# Revit family: Freestanding_Tub-American_Standard-Town_Square-2546004.020
name_source: partatom
category: Plumbing Fixtures
units: mm (PartAtom-declared; Revit-internal decimal feet)

## family parameters
Always vertical = No
Cut with Voids When Loaded = No
OmniClass Number = 23.45.05.14.21
OmniClass Title = Bathtubs
Part Type = Normal
Room Calculation Point = No
Round Connector Dimension = Use Diameter
Shared = Yes
Work Plane-Based = Yes

## types (1)
- 2546004.020
    Assembly Code = D2010510
    CSA B45.5-11 = Yes
    CW Connection = Yes
    CWFU = 3
    Cold Water Connection Diameter = 1/2"
    Default Elevation = 0"
    Description = Town Square® S Freestanding Tub High Gloss Acrylic
    Finish = High Gloss Acrylic-American Standard-020-White
    HW Connection = Yes
    HWFU = 3
    Height = 24 7/16"
    Hot Water Connection Diameter = 1/2"
    IAPMO Z124 = Yes
    Installation Type = Floor Mounted
    Length = 68"
    Manufacturer = American Standard
    Material = High Gloss Acrylic-American Standard-020-White
    Model = 2546004.020
    Price = Prices may vary. Please consult Manufacturer Representative for most up-to-date price list.
    Product Documentation Link = https://americanstandard.box.com
    Product Page URL = https://www.americanstandard-us.com
    Revised Date = 02/09/2022
    Shower = Yes
    Shower Connection Size = 1/2"
    Shower Width = 6"
    Shower void = 24 27/32"
    Supply Width = 4"
    Type Comments = Deck mount filler and overflow cover sold separately
    URL = https://www.americanstandard-us.com
    Vent Connection = No
    WFU = 4
    Warranty Information = Limited Lifetime Warranty
    Waste Connection = Yes
    Waste Connection Diameter = 2 3/16"
    Weight (kg) = 163 Lbs. (74 Kg.)-782 Lbs. (355 Kg.)
    Width = 36"

## geometry (parser evidence)
native form markers: Sweep x2
no freeform markers — native parametric forms only
